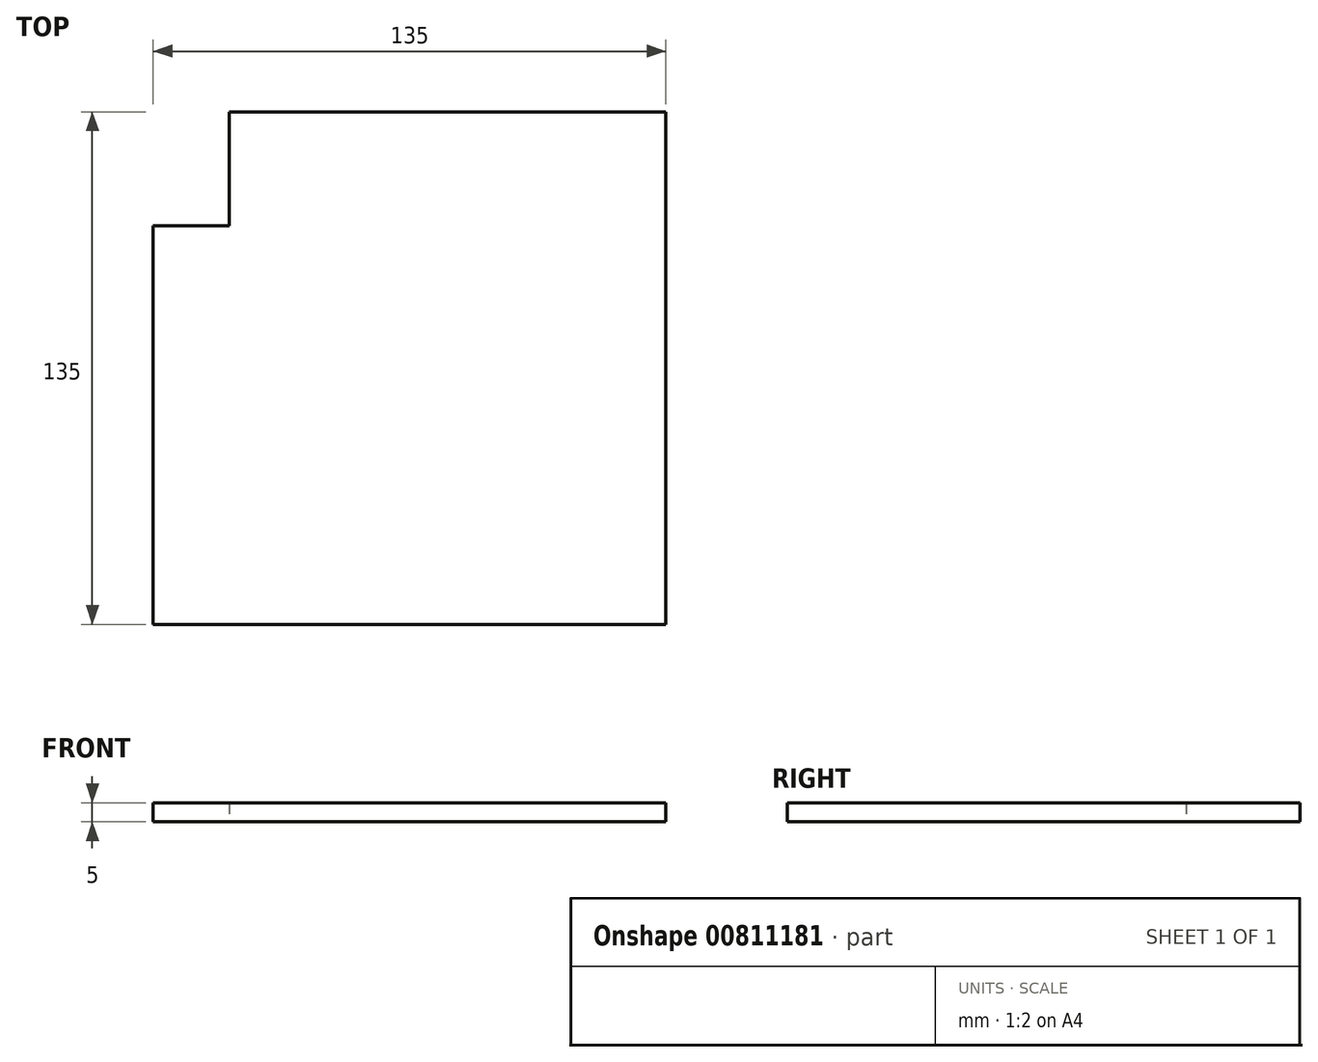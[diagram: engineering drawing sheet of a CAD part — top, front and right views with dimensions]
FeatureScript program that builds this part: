
annotation { "Feature Type Name" : "Feature", "Feature Type Description" : "" }
export const myFeature = defineFeature(function(context is Context, id is Id, definition is map)
    precondition{}
    {
        {
            var Q0;
            Q0=qCreatedBy(makeId("Top.planeOp"),FACE);
            var sketch = newSketch(context, id + "F0", { "sketchPlane" : qUnion([Q0])});
            skLineSegment(sketch, "E0.bottom", {"start": v(-67.5, 67.5) * mm, "end": v(67.5, 67.5) * mm});
            skLineSegment(sketch, "E0.top", {"start": v(-67.5, -67.5) * mm, "end": v(67.5, -67.5) * mm});
            skLineSegment(sketch, "E0.left", {"start": v(-67.5, 67.5) * mm, "end": v(-67.5, -67.5) * mm});
            skLineSegment(sketch, "E0.right", {"start": v(67.5, 67.5) * mm, "end": v(67.5, -67.5) * mm});
            skPoint(sketch, "E0.middle", {"position": v(0, 0) * mm});
            skLineSegment(sketch, "E1", {"start": v(-47.5, 67.5) * mm, "end": v(-47.5, 37.5) * mm});
            skLineSegment(sketch, "E2", {"start": v(-47.5, 37.5) * mm, "end": v(-67.5, 37.5) * mm});
            skSolve(sketch);
        }
        {
            var Q0;
            {var subQ2=sQuery(id+"F0.wireOp",EDGE,"E0.top");Q0=makeQuery(id+"F0.imprint","IMPRINT",FACE,{"disambiguationData":[TD([[makeQuery(id+"F0.imprint","IMPRINT",EDGE,{"derivedFrom":subQ2}),1.0]])]});}
            extrude(context, id + "F1", {"entities" : qUnion([Q0]), "depth" : 5 * mm, "offsetDistance" : 25 * mm});
        }
    });
